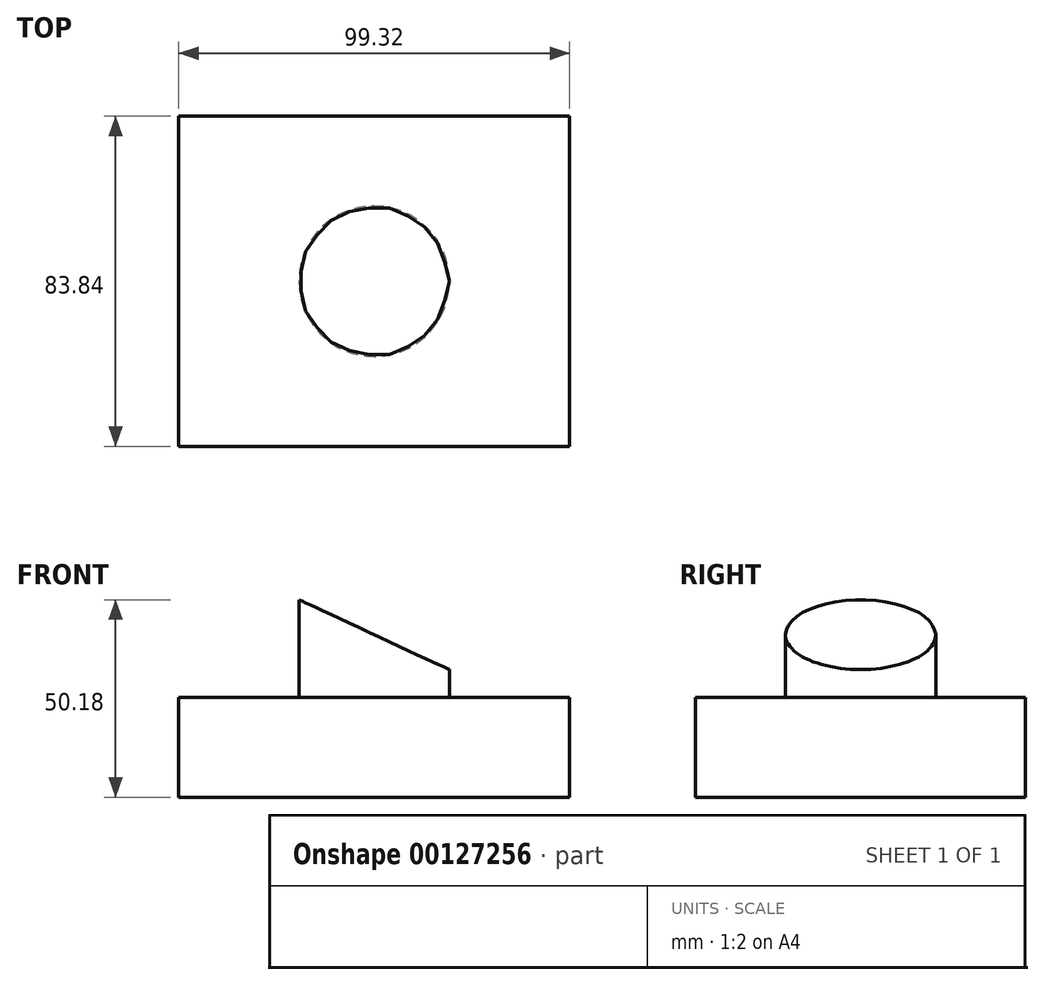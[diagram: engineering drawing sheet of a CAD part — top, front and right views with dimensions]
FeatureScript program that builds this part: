
annotation { "Feature Type Name" : "Feature", "Feature Type Description" : "" }
export const myFeature = defineFeature(function(context is Context, id is Id, definition is map)
    precondition{}
    {
        {
            var Q0;
            Q0=qCreatedBy(makeId("Top.planeOp"),FACE);
            var sketch = newSketch(context, id + "F0", { "sketchPlane" : qUnion([Q0])});
            skLineSegment(sketch, "E0.bottom", {"start": v(49.66, -41.92) * mm, "end": v(-49.66, -41.92) * mm});
            skLineSegment(sketch, "E0.top", {"start": v(49.66, 41.92) * mm, "end": v(-49.66, 41.92) * mm});
            skLineSegment(sketch, "E0.left", {"start": v(49.66, -41.92) * mm, "end": v(49.66, 41.92) * mm});
            skLineSegment(sketch, "E0.right", {"start": v(-49.66, -41.92) * mm, "end": v(-49.66, 41.92) * mm});
            skPoint(sketch, "E0.middle", {"position": v(0, 0) * mm});
            skSolve(sketch);
        }
        {
            var Q0;
            Q0=makeQuery(id+"F0.imprint","IMPRINT",FACE,{"disambiguationData":[TD([[makeQuery(id+"F0.imprint","IMPRINT",EDGE,{"derivedFrom":sQuery(id+"F0.wireOp",EDGE,"E0.bottom")}),-1.0]])]});
            extrude(context, id + "F1", {"entities" : qUnion([Q0]), "depth" : 25.4 * mm});
        }
        {
            var Q0;
            Q0=makeQuery(id+"F1.opExtrude","CAP_FACE",FACE,{"disambiguationData":[OSD([sQuery(id+"F0.wireOp",EDGE,"E0.bottom"),sQuery(id+"F0.wireOp",EDGE,"E0.top"),sQuery(id+"F0.wireOp",EDGE,"E0.left"),sQuery(id+"F0.wireOp",EDGE,"E0.right")])],"isStart":false});
            var sketch = newSketch(context, id + "F2", { "sketchPlane" : qUnion([Q0])});
            skCircle(sketch, "E1", {"center": v(0, 0) * mm, "radius": 19.1 * mm});
            skSolve(sketch);
        }
        {
            var Q0;
            Q0=makeQuery(id+"F2.imprint","IMPRINT",FACE,{"disambiguationData":[TD([[makeQuery(id+"F2.imprint","IMPRINT",EDGE,{"derivedFrom":sQuery(id+"F2.wireOp",EDGE,"E1")}),1.0]])]});
            extrude(context, id + "F3", {"entities" : qUnion([Q0]), "operationType" : NewBodyOperationType.ADD, "depth" : 25.4 * mm});
        }
        {
            var Q0;
            Q0=qCreatedBy(makeId("Front.planeOp"),FACE);
            var sketch = newSketch(context, id + "F4", { "sketchPlane" : qUnion([Q0])});
            skLineSegment(sketch, "E2", {"start": v(-26.07, 53.42) * mm, "end": v(21.9, 53.42) * mm});
            skLineSegment(sketch, "E3", {"start": v(21.9, 53.42) * mm, "end": v(21.9, 31.13) * mm});
            skLineSegment(sketch, "E4", {"start": v(21.9, 31.13) * mm, "end": v(-26.07, 53.42) * mm});
            skSolve(sketch);
        }
        {
            var Q0;
            Q0 = qSketchRegion(id + "F4", true);
            extrude(context, id + "F5", {"entities" : qUnion([Q0]), "operationType" : NewBodyOperationType.REMOVE, "depth" : 88.72 * mm, "symmetric" : true});
        }
    });
